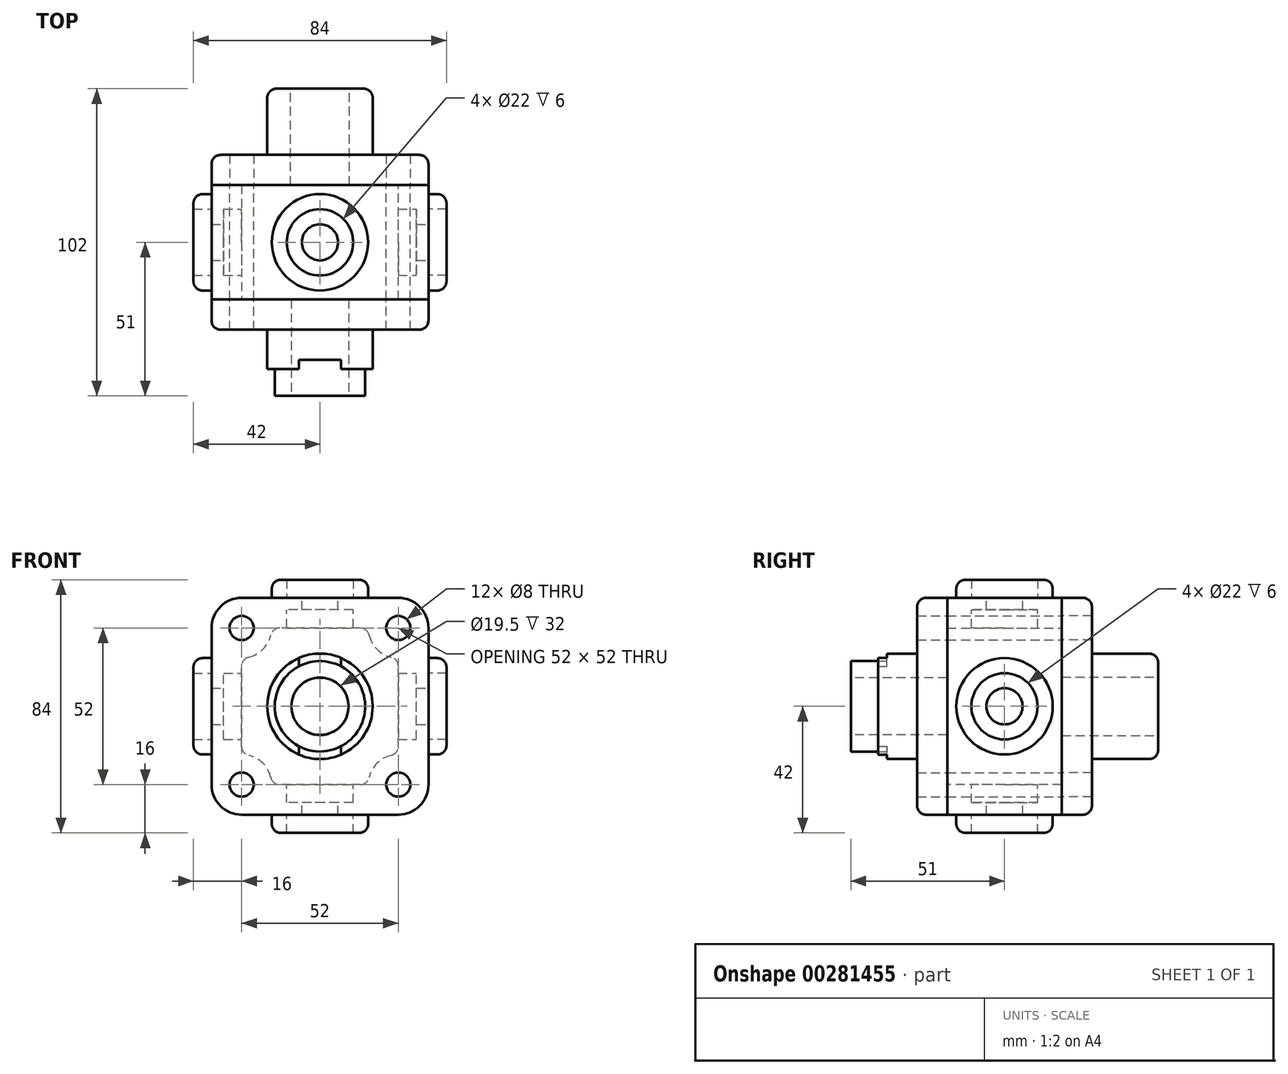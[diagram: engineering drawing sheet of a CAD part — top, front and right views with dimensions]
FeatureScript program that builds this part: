
annotation { "Feature Type Name" : "Feature", "Feature Type Description" : "" }
export const myFeature = defineFeature(function(context is Context, id is Id, definition is map)
    precondition{}
    {
        {
            var Q0;
            Q0=qCreatedBy(makeId("Front.planeOp"),FACE);
            var sketch = newSketch(context, id + "F0", { "sketchPlane" : qUnion([Q0])});
            skLineSegment(sketch, "E0.bottom", {"start": v(26, -26) * mm, "end": v(-26, -26) * mm});
            skLineSegment(sketch, "E0.top", {"start": v(26, 26) * mm, "end": v(-26, 26) * mm});
            skLineSegment(sketch, "E0.left", {"start": v(26, -26) * mm, "end": v(26, 26) * mm});
            skLineSegment(sketch, "E0.right", {"start": v(-26, -26) * mm, "end": v(-26, 26) * mm});
            skPoint(sketch, "E0.middle", {"position": v(0, 0) * mm});
            skLineSegment(sketch, "E1.bottom", {"start": v(-36, -36) * mm, "end": v(36, -36) * mm});
            skLineSegment(sketch, "E1.top", {"start": v(-36, 36) * mm, "end": v(36, 36) * mm});
            skLineSegment(sketch, "E1.left", {"start": v(-36, -36) * mm, "end": v(-36, 36) * mm});
            skLineSegment(sketch, "E1.right", {"start": v(36, -36) * mm, "end": v(36, 36) * mm});
            skCircle(sketch, "E2", {"center": v(26, 26) * mm, "radius": 10 * mm});
            skCircle(sketch, "E3", {"center": v(-26, 26) * mm, "radius": 10 * mm});
            skCircle(sketch, "E4", {"center": v(-26, -26) * mm, "radius": 10 * mm});
            skCircle(sketch, "E5", {"center": v(26, -26) * mm, "radius": 10 * mm});
            skLineSegment(sketch, "E6", {"start": v(36, 36) * mm, "end": v(-36, -36) * mm, "construction": true});
            skLineSegment(sketch, "E7", {"start": v(36, -36) * mm, "end": v(-36, 36) * mm, "construction": true});
            skCircle(sketch, "E8", {"center": v(26, 26) * mm, "radius": 4 * mm});
            skCircle(sketch, "E9", {"center": v(-26, 26) * mm, "radius": 4 * mm});
            skCircle(sketch, "E10", {"center": v(-26, -26) * mm, "radius": 4 * mm});
            skCircle(sketch, "E11", {"center": v(26, -26) * mm, "radius": 4 * mm});
            skLineSegment(sketch, "E12", {"start": v(-72.63, 0) * mm, "end": v(73.83, 0) * mm, "construction": true});
            skLineSegment(sketch, "E13", {"start": v(0, -65.86) * mm, "end": v(0, 72.71) * mm, "construction": true});
            skSolve(sketch);
        }
        {
            var Q0;
            {var subQ0=sQuery(id+"F0.wireOp",EDGE,"E5");var subQ3=makeQuery(id+"F0.imprint","INTERSECT",VERTEX,{"derivedFrom":[sQuery(id+"F0.wireOp",EDGE,"E1.bottom"),subQ0]});Q0=makeQuery(id+"F0.imprint","IMPRINT",FACE,{"disambiguationData":[TD([[makeQuery(id+"F0.imprint","IMPRINT",EDGE,{"disambiguationData":[TD([[subQ3,-1.0]])],"derivedFrom":subQ0}),1.0]])]});}
            var Q1;
            {var subQ0=sQuery(id+"F0.wireOp",EDGE,"E4");var subQ1=sQuery(id+"F0.wireOp",EDGE,"E1.bottom");var subQ2=makeQuery(id+"F0.imprint","INTERSECT",VERTEX,{"derivedFrom":[subQ1,subQ0]});Q1=makeQuery(id+"F0.imprint","IMPRINT",FACE,{"disambiguationData":[TD([[makeQuery(id+"F0.imprint","IMPRINT",EDGE,{"disambiguationData":[TD([[subQ2,-1.0]])],"derivedFrom":subQ1}),1.0]])]});}
            var Q2;
            {var subQ5=sQuery(id+"F0.wireOp",EDGE,"2c42fa13-fa19-4489-94e4-404aec46edff.top");Q2=makeQuery(id+"F0.imprint","IMPRINT",FACE,{"disambiguationData":[TD([[makeQuery(id+"F0.imprint","IMPRINT",EDGE,{"derivedFrom":subQ5}),1.0]])]});}
            var Q3;
            {var subQ5=sQuery(id+"F0.wireOp",EDGE,"ed80a6a9-9b49-4b89-9adc-e16e461cd2ad.left");Q3=makeQuery(id+"F0.imprint","IMPRINT",FACE,{"disambiguationData":[TD([[makeQuery(id+"F0.imprint","IMPRINT",EDGE,{"derivedFrom":subQ5}),1.0]])]});}
            var Q4;
            {var subQ0=sQuery(id+"F0.wireOp",EDGE,"E3");var subQ1=sQuery(id+"F0.wireOp",EDGE,"E1.top");var subQ2=makeQuery(id+"F0.imprint","INTERSECT",VERTEX,{"derivedFrom":[subQ1,subQ0]});Q4=makeQuery(id+"F0.imprint","IMPRINT",FACE,{"disambiguationData":[TD([[makeQuery(id+"F0.imprint","IMPRINT",EDGE,{"disambiguationData":[TD([[subQ2,-1.0]])],"derivedFrom":subQ1}),-1.0]])]});}
            var Q5;
            {var subQ0=sQuery(id+"F0.wireOp",EDGE,"E2");var subQ3=makeQuery(id+"F0.imprint","INTERSECT",VERTEX,{"derivedFrom":[sQuery(id+"F0.wireOp",EDGE,"E1.top"),subQ0]});Q5=makeQuery(id+"F0.imprint","IMPRINT",FACE,{"disambiguationData":[TD([[makeQuery(id+"F0.imprint","IMPRINT",EDGE,{"disambiguationData":[TD([[subQ3,1.0]])],"derivedFrom":subQ0}),1.0]])]});}
            var Q6;
            {var subQ5=sQuery(id+"F0.wireOp",EDGE,"43d30307-da37-4a26-9242-e517d63e6419.top");Q6=makeQuery(id+"F0.imprint","IMPRINT",FACE,{"disambiguationData":[TD([[makeQuery(id+"F0.imprint","IMPRINT",EDGE,{"derivedFrom":subQ5}),-1.0]])]});}
            var Q7;
            {var subQ0=sQuery(id+"F0.wireOp",EDGE,"E3");var subQ3=makeQuery(id+"F0.imprint","INTERSECT",VERTEX,{"derivedFrom":[sQuery(id+"F0.wireOp",EDGE,"E1.top"),subQ0]});Q7=makeQuery(id+"F0.imprint","IMPRINT",FACE,{"disambiguationData":[TD([[makeQuery(id+"F0.imprint","IMPRINT",EDGE,{"disambiguationData":[TD([[subQ3,-1.0]])],"derivedFrom":subQ0}),1.0]])]});}
            var Q8;
            {var subQ0=sQuery(id+"F0.wireOp",EDGE,"E4");var subQ1=sQuery(id+"F0.wireOp",EDGE,"E1.left");var subQ2=makeQuery(id+"F0.imprint","INTERSECT",VERTEX,{"derivedFrom":[subQ1,subQ0]});Q8=makeQuery(id+"F0.imprint","IMPRINT",FACE,{"disambiguationData":[TD([[makeQuery(id+"F0.imprint","IMPRINT",EDGE,{"disambiguationData":[TD([[subQ2,-1.0]])],"derivedFrom":subQ1}),-1.0]])]});}
            var Q9;
            {var subQ0=sQuery(id+"F0.wireOp",EDGE,"d46692bc-23da-4b0a-9166-fa2d0df1a2c0.right");Q9=makeQuery(id+"F0.imprint","IMPRINT",FACE,{"disambiguationData":[TD([[makeQuery(id+"F0.imprint","IMPRINT",EDGE,{"derivedFrom":subQ0}),1.0]])]});}
            var Q10;
            {var subQ0=sQuery(id+"F0.wireOp",EDGE,"E5");var subQ1=sQuery(id+"F0.wireOp",EDGE,"E1.right");var subQ2=makeQuery(id+"F0.imprint","INTERSECT",VERTEX,{"derivedFrom":[subQ1,subQ0]});Q10=makeQuery(id+"F0.imprint","IMPRINT",FACE,{"disambiguationData":[TD([[makeQuery(id+"F0.imprint","IMPRINT",EDGE,{"disambiguationData":[TD([[subQ2,-1.0]])],"derivedFrom":subQ1}),1.0]])]});}
            var Q11;
            {var subQ0=sQuery(id+"F0.wireOp",EDGE,"E4");var subQ1=makeQuery(id+"F0.imprint","INTERSECT",VERTEX,{"derivedFrom":[sQuery(id+"F0.wireOp",EDGE,"E1.bottom"),subQ0]});Q11=makeQuery(id+"F0.imprint","IMPRINT",FACE,{"disambiguationData":[TD([[makeQuery(id+"F0.imprint","IMPRINT",EDGE,{"disambiguationData":[TD([[subQ1,1.0]])],"derivedFrom":subQ0}),1.0]])]});}
            var Q12;
            {var subQ5=sQuery(id+"F0.wireOp",EDGE,"2c42fa13-fa19-4489-94e4-404aec46edff.bottom");Q12=makeQuery(id+"F0.imprint","IMPRINT",FACE,{"disambiguationData":[TD([[makeQuery(id+"F0.imprint","IMPRINT",EDGE,{"derivedFrom":subQ5}),-1.0]])]});}
            var Q13;
            {var subQ5=sQuery(id+"F0.wireOp",EDGE,"ed80a6a9-9b49-4b89-9adc-e16e461cd2ad.right");Q13=makeQuery(id+"F0.imprint","IMPRINT",FACE,{"disambiguationData":[TD([[makeQuery(id+"F0.imprint","IMPRINT",EDGE,{"derivedFrom":subQ5}),-1.0]])]});}
            var Q14;
            {var subQ5=sQuery(id+"F0.wireOp",EDGE,"d46692bc-23da-4b0a-9166-fa2d0df1a2c0.left");Q14=makeQuery(id+"F0.imprint","IMPRINT",FACE,{"disambiguationData":[TD([[makeQuery(id+"F0.imprint","IMPRINT",EDGE,{"derivedFrom":subQ5}),-1.0]])]});}
            var Q15;
            {var subQ5=sQuery(id+"F0.wireOp",EDGE,"43d30307-da37-4a26-9242-e517d63e6419.bottom");Q15=makeQuery(id+"F0.imprint","IMPRINT",FACE,{"disambiguationData":[TD([[makeQuery(id+"F0.imprint","IMPRINT",EDGE,{"derivedFrom":subQ5}),1.0]])]});}
            var Q16;
            {var subQ1=sQuery(id+"F0.wireOp",EDGE,"E0.top");var subQ3=sQuery(id+"F0.wireOp",EDGE,"E9");var subQ4=makeQuery(id+"F0.imprint","INTERSECT",VERTEX,{"derivedFrom":[subQ1,subQ3]});Q16=makeQuery(id+"F0.imprint","IMPRINT",FACE,{"disambiguationData":[TD([[makeQuery(id+"F0.imprint","IMPRINT",EDGE,{"disambiguationData":[TD([[subQ4,1.0]])],"derivedFrom":subQ3}),-1.0]])]});}
            var Q17;
            {var subQ1=sQuery(id+"F0.wireOp",EDGE,"E0.bottom");var subQ3=sQuery(id+"F0.wireOp",EDGE,"E10");var subQ4=makeQuery(id+"F0.imprint","INTERSECT",VERTEX,{"derivedFrom":[subQ1,subQ3]});Q17=makeQuery(id+"F0.imprint","IMPRINT",FACE,{"disambiguationData":[TD([[makeQuery(id+"F0.imprint","IMPRINT",EDGE,{"disambiguationData":[TD([[subQ4,-1.0]])],"derivedFrom":subQ3}),-1.0]])]});}
            var Q18;
            {var subQ1=sQuery(id+"F0.wireOp",EDGE,"E0.bottom");var subQ3=sQuery(id+"F0.wireOp",EDGE,"E11");var subQ4=makeQuery(id+"F0.imprint","INTERSECT",VERTEX,{"derivedFrom":[subQ1,subQ3]});Q18=makeQuery(id+"F0.imprint","IMPRINT",FACE,{"disambiguationData":[TD([[makeQuery(id+"F0.imprint","IMPRINT",EDGE,{"disambiguationData":[TD([[subQ4,1.0]])],"derivedFrom":subQ3}),-1.0]])]});}
            var Q19;
            {var subQ1=sQuery(id+"F0.wireOp",EDGE,"E0.top");var subQ3=sQuery(id+"F0.wireOp",EDGE,"E8");var subQ4=makeQuery(id+"F0.imprint","INTERSECT",VERTEX,{"derivedFrom":[subQ1,subQ3]});Q19=makeQuery(id+"F0.imprint","IMPRINT",FACE,{"disambiguationData":[TD([[makeQuery(id+"F0.imprint","IMPRINT",EDGE,{"disambiguationData":[TD([[subQ4,-1.0]])],"derivedFrom":subQ3}),-1.0]])]});}
            extrude(context, id + "F1", {"entities" : qUnion([Q0, Q1, Q2, Q3, Q4, Q5, Q6, Q7, Q8, Q9, Q10, Q11, Q12, Q13, Q14, Q15, Q16, Q17, Q18, Q19]), "endBound" : BoundingType.SYMMETRIC, "depth" : 38 * mm});
        }
        {
            var Q0;
            Q0=qCreatedBy(makeId("Right.planeOp"),FACE);
            var sketch = newSketch(context, id + "F2", { "sketchPlane" : qUnion([Q0])});
            skCircle(sketch, "E14", {"center": v(0, 0) * mm, "radius": 11 * mm});
            skCircle(sketch, "E15", {"center": v(0, 0) * mm, "radius": 6 * mm});
            skSolve(sketch);
        }
        {
            var Q0;
            Q0=makeQuery(id+"F2.imprint","IMPRINT",FACE,{"disambiguationData":[TD([[makeQuery(id+"F2.imprint","IMPRINT",EDGE,{"derivedFrom":sQuery(id+"F2.wireOp",EDGE,"E15")}),1.0]])]});
            extrude(context, id + "F3", {"entities" : qUnion([Q0]), "operationType" : NewBodyOperationType.REMOVE, "endBound" : BoundingType.SYMMETRIC, "oppositeDirection" : true, "depth" : 80 * mm});
        }
        {
            var Q0;
            Q0=makeQuery(id+"F2.imprint","IMPRINT",FACE,{"disambiguationData":[TD([[makeQuery(id+"F2.imprint","IMPRINT",EDGE,{"derivedFrom":sQuery(id+"F2.wireOp",EDGE,"E14")}),1.0]])]});
            extrude(context, id + "F4", {"entities" : qUnion([Q0]), "operationType" : NewBodyOperationType.REMOVE, "endBound" : BoundingType.SYMMETRIC, "oppositeDirection" : true, "depth" : 64 * mm});
        }
        {
            var Q0;
            Q0=makeQuery(id+"F1.opExtrude","SWEPT_FACE",FACE,{"disambiguationData":[OSD([sQuery(id+"F0.wireOp",EDGE,"E1.left")])]});
            var sketch = newSketch(context, id + "F5", { "sketchPlane" : qUnion([Q0])});
            skCircle(sketch, "E16", {"center": v(0, 0) * mm, "radius": 11 * mm});
            skCircle(sketch, "E17", {"center": v(0, 0) * mm, "radius": 16 * mm});
            skSolve(sketch);
        }
        {
            var Q0;
            Q0=makeQuery(id+"F5.imprint","IMPRINT",FACE,{"disambiguationData":[TD([[makeQuery(id+"F5.imprint","IMPRINT",EDGE,{"derivedFrom":sQuery(id+"F5.wireOp",EDGE,"E16")}),-1.0]])]});
            extrude(context, id + "F6", {"entities" : qUnion([Q0]), "operationType" : NewBodyOperationType.ADD, "depth" : 6 * mm});
        }
        {
            var Q0;
            Q0=makeQuery(id+"F1.opExtrude","SWEPT_FACE",FACE,{"disambiguationData":[OSD([sQuery(id+"F0.wireOp",EDGE,"E1.right")])]});
            var sketch = newSketch(context, id + "F7", { "sketchPlane" : qUnion([Q0])});
            skCircle(sketch, "E18", {"center": v(0, 0) * mm, "radius": 11 * mm});
            skCircle(sketch, "E19", {"center": v(0, 0) * mm, "radius": 16 * mm});
            skSolve(sketch);
        }
        {
            var Q0;
            Q0=makeQuery(id+"F7.imprint","IMPRINT",FACE,{"disambiguationData":[TD([[makeQuery(id+"F7.imprint","IMPRINT",EDGE,{"derivedFrom":sQuery(id+"F7.wireOp",EDGE,"E18")}),-1.0]])]});
            extrude(context, id + "F8", {"entities" : qUnion([Q0]), "operationType" : NewBodyOperationType.ADD, "depth" : 6 * mm});
        }
        {
            var Q0;
            Q0=qCreatedBy(makeId("Top.planeOp"),FACE);
            var sketch = newSketch(context, id + "F9", { "sketchPlane" : qUnion([Q0])});
            skCircle(sketch, "E20", {"center": v(0, 0) * mm, "radius": 6 * mm});
            skCircle(sketch, "E21", {"center": v(0, 0) * mm, "radius": 11 * mm});
            skSolve(sketch);
        }
        {
            var Q0;
            Q0=makeQuery(id+"F9.imprint","IMPRINT",FACE,{"disambiguationData":[TD([[makeQuery(id+"F9.imprint","IMPRINT",EDGE,{"derivedFrom":sQuery(id+"F9.wireOp",EDGE,"E20")}),1.0]])]});
            extrude(context, id + "F10", {"entities" : qUnion([Q0]), "operationType" : NewBodyOperationType.REMOVE, "endBound" : BoundingType.SYMMETRIC, "oppositeDirection" : true, "depth" : 80 * mm});
        }
        {
            var Q0;
            Q0=makeQuery(id+"F9.imprint","IMPRINT",FACE,{"disambiguationData":[TD([[makeQuery(id+"F9.imprint","IMPRINT",EDGE,{"derivedFrom":sQuery(id+"F9.wireOp",EDGE,"E20")}),-1.0]])]});
            extrude(context, id + "F11", {"entities" : qUnion([Q0]), "operationType" : NewBodyOperationType.REMOVE, "endBound" : BoundingType.SYMMETRIC, "oppositeDirection" : true, "depth" : 64 * mm});
        }
        {
            var Q0;
            Q0=makeQuery(id+"F1.opExtrude","SWEPT_FACE",FACE,{"disambiguationData":[OSD([sQuery(id+"F0.wireOp",EDGE,"E1.top")])]});
            var sketch = newSketch(context, id + "F12", { "sketchPlane" : qUnion([Q0])});
            skCircle(sketch, "E22", {"center": v(0, 0) * mm, "radius": 11 * mm});
            skCircle(sketch, "E23", {"center": v(0, 0) * mm, "radius": 16 * mm});
            skSolve(sketch);
        }
        {
            var Q0;
            Q0=makeQuery(id+"F12.imprint","IMPRINT",FACE,{"disambiguationData":[TD([[makeQuery(id+"F12.imprint","IMPRINT",EDGE,{"derivedFrom":sQuery(id+"F12.wireOp",EDGE,"E22")}),-1.0]])]});
            extrude(context, id + "F13", {"entities" : qUnion([Q0]), "operationType" : NewBodyOperationType.ADD, "depth" : 6 * mm});
        }
        {
            var Q0;
            Q0=makeQuery(id+"F1.opExtrude","SWEPT_FACE",FACE,{"disambiguationData":[OSD([sQuery(id+"F0.wireOp",EDGE,"E1.bottom")])]});
            var sketch = newSketch(context, id + "F14", { "sketchPlane" : qUnion([Q0])});
            skCircle(sketch, "E24", {"center": v(0, 0) * mm, "radius": 11 * mm});
            skCircle(sketch, "E25", {"center": v(0, 0) * mm, "radius": 16 * mm});
            skSolve(sketch);
        }
        {
            var Q0;
            Q0=makeQuery(id+"F14.imprint","IMPRINT",FACE,{"disambiguationData":[TD([[makeQuery(id+"F14.imprint","IMPRINT",EDGE,{"derivedFrom":sQuery(id+"F14.wireOp",EDGE,"E24")}),-1.0]])]});
            extrude(context, id + "F15", {"entities" : qUnion([Q0]), "operationType" : NewBodyOperationType.ADD, "depth" : 6 * mm});
        }
        {
            var Q0;
            Q0=makeQuery(id+"F15.opExtrude","CAP_EDGE",EDGE,{"disambiguationData":[OSD([sQuery(id+"F14.wireOp",EDGE,"E25")])],"isStart":true});
            var Q1;
            Q1=makeQuery(id+"F6.opExtrude","CAP_EDGE",EDGE,{"disambiguationData":[OSD([sQuery(id+"F5.wireOp",EDGE,"E17")])],"isStart":true});
            var Q2;
            Q2=makeQuery(id+"F8.opExtrude","CAP_EDGE",EDGE,{"disambiguationData":[OSD([sQuery(id+"F7.wireOp",EDGE,"E19")])],"isStart":true});
            var Q3;
            Q3=makeQuery(id+"F13.opExtrude","CAP_EDGE",EDGE,{"disambiguationData":[OSD([sQuery(id+"F12.wireOp",EDGE,"E23")])],"isStart":true});
            var Q4;
            Q4=makeQuery(id+"F1.opExtrude","SWEPT_EDGE",EDGE,{"disambiguationData":[OSD([sQuery(id+"F0.wireOp",EDGE,"E0.right"),sQuery(id+"F0.wireOp",EDGE,"E4")])]});
            var Q5;
            Q5=makeQuery(id+"F1.opExtrude","SWEPT_EDGE",EDGE,{"disambiguationData":[OSD([sQuery(id+"F0.wireOp",EDGE,"E0.bottom"),sQuery(id+"F0.wireOp",EDGE,"E4")])]});
            var Q6;
            Q6=makeQuery(id+"F1.opExtrude","SWEPT_EDGE",EDGE,{"disambiguationData":[OSD([sQuery(id+"F0.wireOp",EDGE,"E0.left"),sQuery(id+"F0.wireOp",EDGE,"E5")])]});
            var Q7;
            Q7=makeQuery(id+"F1.opExtrude","SWEPT_EDGE",EDGE,{"disambiguationData":[OSD([sQuery(id+"F0.wireOp",EDGE,"E0.bottom"),sQuery(id+"F0.wireOp",EDGE,"E5")])]});
            var Q8;
            Q8=makeQuery(id+"F1.opExtrude","SWEPT_EDGE",EDGE,{"disambiguationData":[OSD([sQuery(id+"F0.wireOp",EDGE,"E0.left"),sQuery(id+"F0.wireOp",EDGE,"E2")])]});
            var Q9;
            Q9=makeQuery(id+"F1.opExtrude","SWEPT_EDGE",EDGE,{"disambiguationData":[OSD([sQuery(id+"F0.wireOp",EDGE,"E0.top"),sQuery(id+"F0.wireOp",EDGE,"E2")])]});
            var Q10;
            Q10=makeQuery(id+"F1.opExtrude","SWEPT_EDGE",EDGE,{"disambiguationData":[OSD([sQuery(id+"F0.wireOp",EDGE,"E0.top"),sQuery(id+"F0.wireOp",EDGE,"E3")])]});
            var Q11;
            Q11=makeQuery(id+"F1.opExtrude","SWEPT_EDGE",EDGE,{"disambiguationData":[OSD([sQuery(id+"F0.wireOp",EDGE,"E0.right"),sQuery(id+"F0.wireOp",EDGE,"E3")])]});
            var Q12;
            Q12=makeQuery(id+"F8.opExtrude","CAP_EDGE",EDGE,{"disambiguationData":[OSD([sQuery(id+"F7.wireOp",EDGE,"E19")])],"isStart":false});
            var Q13;
            Q13=makeQuery(id+"F15.opExtrude","CAP_EDGE",EDGE,{"disambiguationData":[OSD([sQuery(id+"F14.wireOp",EDGE,"E25")])],"isStart":false});
            var Q14;
            Q14=makeQuery(id+"F13.opExtrude","CAP_EDGE",EDGE,{"disambiguationData":[OSD([sQuery(id+"F12.wireOp",EDGE,"E23")])],"isStart":false});
            var Q15;
            Q15=makeQuery(id+"F6.opExtrude","CAP_EDGE",EDGE,{"disambiguationData":[OSD([sQuery(id+"F5.wireOp",EDGE,"E17")])],"isStart":false});
            fillet(context, id + "F16", {"entities" : qUnion([Q0, Q1, Q2, Q3, Q4, Q5, Q6, Q7, Q8, Q9, Q10, Q11, Q12, Q13, Q14, Q15]), "radius" : 3 * mm, "tangentPropagation" : true, "allowEdgeOverflow" : false});
        }
        {
            var Q0;
            Q0=makeQuery(id+"F1.opExtrude","CAP_FACE",FACE,{"disambiguationData":[OSD([sQuery(id+"F0.wireOp",EDGE,"E0.bottom"),sQuery(id+"F0.wireOp",EDGE,"E0.top"),sQuery(id+"F0.wireOp",EDGE,"E0.left"),sQuery(id+"F0.wireOp",EDGE,"E0.right"),sQuery(id+"F0.wireOp",EDGE,"E1.bottom"),sQuery(id+"F0.wireOp",EDGE,"E1.top"),sQuery(id+"F0.wireOp",EDGE,"E1.left"),sQuery(id+"F0.wireOp",EDGE,"E1.right"),sQuery(id+"F0.wireOp",EDGE,"E2"),sQuery(id+"F0.wireOp",EDGE,"E3"),sQuery(id+"F0.wireOp",EDGE,"E4"),sQuery(id+"F0.wireOp",EDGE,"E5"),sQuery(id+"F0.wireOp",EDGE,"E8"),sQuery(id+"F0.wireOp",EDGE,"E9"),sQuery(id+"F0.wireOp",EDGE,"E10"),sQuery(id+"F0.wireOp",EDGE,"E11")])],"isStart":false});
            var sketch = newSketch(context, id + "F17", { "sketchPlane" : qUnion([Q0])});
            skSolve(sketch);
        }
        {
            var Q0;
            {var subQ1=sQuery(id+"F0.wireOp",EDGE,"E0.bottom");Q0=makeQuery(id+"F17.imprint","IMPRINT",FACE,{"disambiguationData":[TD([[makeQuery(id+"F17.imprint","IMPRINT",EDGE,{"derivedFrom":makeQuery(id+"F1.opExtrude","CAP_EDGE",EDGE,{"disambiguationData":[OSD([subQ1])],"isStart":false})}),-1.0]])]});}
            var Q1;
            {var subQ11=sQuery(id+"F0.wireOp",EDGE,"E8");Q1=makeQuery(id+"F17.imprint","IMPRINT",FACE,{"disambiguationData":[TD([[makeQuery(id+"F17.imprint","IMPRINT",EDGE,{"derivedFrom":makeQuery(id+"F1.opExtrude","CAP_EDGE",EDGE,{"disambiguationData":[OSD([subQ11])],"isStart":false})}),-1.0]])]});}
            extrude(context, id + "F18", {"entities" : qUnion([Q0, Q1]), "depth" : 10 * mm});
        }
        {
            var Q0;
            Q0=makeQuery(id+"F18.opExtrude","CAP_FACE",FACE,{"disambiguationData":[OSD([sQuery(id+"F0.wireOp",EDGE,"E1.bottom"),sQuery(id+"F0.wireOp",EDGE,"E1.top"),sQuery(id+"F0.wireOp",EDGE,"E1.left"),sQuery(id+"F0.wireOp",EDGE,"E1.right"),sQuery(id+"F0.wireOp",EDGE,"E2"),sQuery(id+"F0.wireOp",EDGE,"E3"),sQuery(id+"F0.wireOp",EDGE,"E4"),sQuery(id+"F0.wireOp",EDGE,"E5"),sQuery(id+"F0.wireOp",EDGE,"E8"),sQuery(id+"F0.wireOp",EDGE,"E9"),sQuery(id+"F0.wireOp",EDGE,"E10"),sQuery(id+"F0.wireOp",EDGE,"E11")])],"isStart":false});
            var sketch = newSketch(context, id + "F19", { "sketchPlane" : qUnion([Q0])});
            skCircle(sketch, "E26", {"center": v(0, 0) * mm, "radius": 9.5 * mm});
            skCircle(sketch, "E27", {"center": v(0, 0) * mm, "radius": 15 * mm});
            skCircle(sketch, "E28", {"center": v(0, 0) * mm, "radius": 17.5 * mm});
            skSolve(sketch);
        }
        {
            var Q0;
            Q0=makeQuery(id+"F19.imprint","IMPRINT",FACE,{"disambiguationData":[TD([[makeQuery(id+"F19.imprint","IMPRINT",EDGE,{"derivedFrom":sQuery(id+"F19.wireOp",EDGE,"E26")}),1.0]])]});
            extrude(context, id + "F20", {"entities" : qUnion([Q0]), "operationType" : NewBodyOperationType.REMOVE, "oppositeDirection" : true, "depth" : 10 * mm});
        }
        {
            var Q0;
            Q0=makeQuery(id+"F19.imprint","IMPRINT",FACE,{"disambiguationData":[TD([[makeQuery(id+"F19.imprint","IMPRINT",EDGE,{"derivedFrom":sQuery(id+"F19.wireOp",EDGE,"E26")}),1.0]])]});
            extrude(context, id + "F21", {"entities" : qUnion([Q0]), "operationType" : NewBodyOperationType.REMOVE, "oppositeDirection" : true, "depth" : 10 * mm});
        }
        {
            var Q0;
            Q0=makeQuery(id+"F19.imprint","IMPRINT",FACE,{"disambiguationData":[TD([[makeQuery(id+"F19.imprint","IMPRINT",EDGE,{"derivedFrom":sQuery(id+"F19.wireOp",EDGE,"E26")}),-1.0]])]});
            extrude(context, id + "F22", {"entities" : qUnion([Q0]), "operationType" : NewBodyOperationType.ADD, "depth" : 22 * mm});
        }
        {
            var Q0;
            Q0=makeQuery(id+"F19.imprint","IMPRINT",FACE,{"disambiguationData":[TD([[makeQuery(id+"F19.imprint","IMPRINT",EDGE,{"derivedFrom":sQuery(id+"F19.wireOp",EDGE,"E27")}),-1.0]])]});
            extrude(context, id + "F23", {"entities" : qUnion([Q0]), "operationType" : NewBodyOperationType.ADD, "depth" : 10 * mm});
        }
        {
            var Q0;
            Q0=makeQuery(id+"F23.opExtrude","CAP_FACE",FACE,{"disambiguationData":[OSD([sQuery(id+"F19.wireOp",EDGE,"E27"),sQuery(id+"F19.wireOp",EDGE,"E28")])],"isStart":false});
            var sketch = newSketch(context, id + "F24", { "sketchPlane" : qUnion([Q0])});
            skLineSegment(sketch, "E29.bottom", {"start": v(7, -30) * mm, "end": v(-7, -30) * mm});
            skLineSegment(sketch, "E29.top", {"start": v(7, 30) * mm, "end": v(-7, 30) * mm});
            skLineSegment(sketch, "E29.left", {"start": v(7, -30) * mm, "end": v(7, 30) * mm});
            skLineSegment(sketch, "E29.right", {"start": v(-7, -30) * mm, "end": v(-7, 30) * mm});
            skPoint(sketch, "E29.middle", {"position": v(0, 0) * mm});
            skSolve(sketch);
        }
        {
            var Q0;
            {var subQ0=sQuery(id+"F24.wireOp",EDGE,"E29.left");var subQ1=makeQuery(id+"F23.opExtrude","CAP_EDGE",EDGE,{"disambiguationData":[OSD([sQuery(id+"F19.wireOp",EDGE,"E28")])],"isStart":false});var subQ2=makeQuery(id+"F24.imprint","INTERSECT",VERTEX,{"disambiguationData":[OD(0.0)],"derivedFrom":[subQ1,subQ0]});Q0=makeQuery(id+"F24.imprint","IMPRINT",FACE,{"disambiguationData":[TD([[makeQuery(id+"F24.imprint","IMPRINT",EDGE,{"disambiguationData":[TD([[subQ2,-1.0]])],"derivedFrom":subQ0}),-1.0]])]});}
            var Q1;
            {var subQ0=sQuery(id+"F24.wireOp",EDGE,"E29.right");var subQ1=makeQuery(id+"F23.opExtrude","CAP_EDGE",EDGE,{"disambiguationData":[OSD([sQuery(id+"F19.wireOp",EDGE,"E28")])],"isStart":false});var subQ2=makeQuery(id+"F24.imprint","INTERSECT",VERTEX,{"disambiguationData":[OD(0.0)],"derivedFrom":[subQ1,subQ0]});Q1=makeQuery(id+"F24.imprint","IMPRINT",FACE,{"disambiguationData":[TD([[makeQuery(id+"F24.imprint","IMPRINT",EDGE,{"disambiguationData":[TD([[subQ2,-1.0]])],"derivedFrom":subQ0}),1.0]])]});}
            extrude(context, id + "F25", {"entities" : qUnion([Q0, Q1]), "operationType" : NewBodyOperationType.ADD, "depth" : 3 * mm});
        }
        {
            var Q0;
            Q0=makeQuery(id+"F18.opExtrude","CAP_EDGE",EDGE,{"disambiguationData":[OSD([sQuery(id+"F0.wireOp",EDGE,"E1.right")])],"isStart":false});
            var Q1;
            Q1=makeQuery(id+"F18.opExtrude","CAP_EDGE",EDGE,{"disambiguationData":[OSD([sQuery(id+"F0.wireOp",EDGE,"E5")])],"isStart":false});
            var Q2;
            Q2=makeQuery(id+"F18.opExtrude","CAP_EDGE",EDGE,{"disambiguationData":[OSD([sQuery(id+"F0.wireOp",EDGE,"E2")])],"isStart":false});
            var Q3;
            Q3=makeQuery(id+"F18.opExtrude","CAP_EDGE",EDGE,{"disambiguationData":[OSD([sQuery(id+"F0.wireOp",EDGE,"E1.top")])],"isStart":false});
            var Q4;
            Q4=makeQuery(id+"F18.opExtrude","CAP_EDGE",EDGE,{"disambiguationData":[OSD([sQuery(id+"F0.wireOp",EDGE,"E3")])],"isStart":false});
            var Q5;
            Q5=makeQuery(id+"F18.opExtrude","CAP_EDGE",EDGE,{"disambiguationData":[OSD([sQuery(id+"F0.wireOp",EDGE,"E1.left")])],"isStart":false});
            var Q6;
            Q6=makeQuery(id+"F18.opExtrude","CAP_EDGE",EDGE,{"disambiguationData":[OSD([sQuery(id+"F0.wireOp",EDGE,"E1.bottom")])],"isStart":false});
            var Q7;
            Q7=makeQuery(id+"F18.opExtrude","CAP_EDGE",EDGE,{"disambiguationData":[OSD([sQuery(id+"F0.wireOp",EDGE,"E4")])],"isStart":false});
            fillet(context, id + "F26", {"entities" : qUnion([Q0, Q1, Q2, Q3, Q4, Q5, Q6, Q7]), "radius" : 3 * mm, "tangentPropagation" : true, "allowEdgeOverflow" : false});
        }
        {
            var Q0;
            Q0=makeQuery(id+"F1.opExtrude","CAP_FACE",FACE,{"disambiguationData":[OSD([sQuery(id+"F0.wireOp",EDGE,"E0.bottom"),sQuery(id+"F0.wireOp",EDGE,"E0.top"),sQuery(id+"F0.wireOp",EDGE,"E0.left"),sQuery(id+"F0.wireOp",EDGE,"E0.right"),sQuery(id+"F0.wireOp",EDGE,"E1.bottom"),sQuery(id+"F0.wireOp",EDGE,"E1.top"),sQuery(id+"F0.wireOp",EDGE,"E1.left"),sQuery(id+"F0.wireOp",EDGE,"E1.right"),sQuery(id+"F0.wireOp",EDGE,"E2"),sQuery(id+"F0.wireOp",EDGE,"E3"),sQuery(id+"F0.wireOp",EDGE,"E4"),sQuery(id+"F0.wireOp",EDGE,"E5"),sQuery(id+"F0.wireOp",EDGE,"E8"),sQuery(id+"F0.wireOp",EDGE,"E9"),sQuery(id+"F0.wireOp",EDGE,"E10"),sQuery(id+"F0.wireOp",EDGE,"E11")])],"isStart":true});
            var sketch = newSketch(context, id + "F27", { "sketchPlane" : qUnion([Q0])});
            skSolve(sketch);
        }
        {
            var Q0;
            {var subQ11=sQuery(id+"F0.wireOp",EDGE,"E8");Q0=makeQuery(id+"F27.imprint","IMPRINT",FACE,{"disambiguationData":[TD([[makeQuery(id+"F27.imprint","IMPRINT",EDGE,{"derivedFrom":makeQuery(id+"F1.opExtrude","CAP_EDGE",EDGE,{"disambiguationData":[OSD([subQ11])],"isStart":true})}),1.0]])]});}
            var Q1;
            {var subQ1=sQuery(id+"F0.wireOp",EDGE,"E0.bottom");Q1=makeQuery(id+"F27.imprint","IMPRINT",FACE,{"disambiguationData":[TD([[makeQuery(id+"F27.imprint","IMPRINT",EDGE,{"derivedFrom":makeQuery(id+"F1.opExtrude","CAP_EDGE",EDGE,{"disambiguationData":[OSD([subQ1])],"isStart":true})}),1.0]])]});}
            extrude(context, id + "F28", {"entities" : qUnion([Q0, Q1]), "depth" : 10 * mm});
        }
        {
            var Q0;
            Q0=makeQuery(id+"F28.opExtrude","CAP_FACE",FACE,{"disambiguationData":[OSD([sQuery(id+"F0.wireOp",EDGE,"E1.bottom"),sQuery(id+"F0.wireOp",EDGE,"E1.top"),sQuery(id+"F0.wireOp",EDGE,"E1.left"),sQuery(id+"F0.wireOp",EDGE,"E1.right"),sQuery(id+"F0.wireOp",EDGE,"E2"),sQuery(id+"F0.wireOp",EDGE,"E3"),sQuery(id+"F0.wireOp",EDGE,"E4"),sQuery(id+"F0.wireOp",EDGE,"E5"),sQuery(id+"F0.wireOp",EDGE,"E8"),sQuery(id+"F0.wireOp",EDGE,"E9"),sQuery(id+"F0.wireOp",EDGE,"E10"),sQuery(id+"F0.wireOp",EDGE,"E11")])],"isStart":false});
            var sketch = newSketch(context, id + "F29", { "sketchPlane" : qUnion([Q0])});
            skCircle(sketch, "E30", {"center": v(0, 0) * mm, "radius": 9.75 * mm});
            skCircle(sketch, "E31", {"center": v(0, 0) * mm, "radius": 17.5 * mm});
            skSolve(sketch);
        }
        {
            var Q0;
            Q0=makeQuery(id+"F29.imprint","IMPRINT",FACE,{"disambiguationData":[TD([[makeQuery(id+"F29.imprint","IMPRINT",EDGE,{"derivedFrom":sQuery(id+"F29.wireOp",EDGE,"E30")}),1.0]])]});
            extrude(context, id + "F30", {"entities" : qUnion([Q0]), "operationType" : NewBodyOperationType.REMOVE, "oppositeDirection" : true, "depth" : 10 * mm});
        }
        {
            var Q0;
            Q0=makeQuery(id+"F29.imprint","IMPRINT",FACE,{"disambiguationData":[TD([[makeQuery(id+"F29.imprint","IMPRINT",EDGE,{"derivedFrom":sQuery(id+"F29.wireOp",EDGE,"E30")}),-1.0]])]});
            extrude(context, id + "F31", {"entities" : qUnion([Q0]), "operationType" : NewBodyOperationType.ADD, "depth" : 22 * mm});
        }
        {
            var Q0;
            Q0=makeQuery(id+"F28.opExtrude","CAP_EDGE",EDGE,{"disambiguationData":[OSD([sQuery(id+"F0.wireOp",EDGE,"E1.left")])],"isStart":false});
            var Q1;
            Q1=makeQuery(id+"F28.opExtrude","CAP_EDGE",EDGE,{"disambiguationData":[OSD([sQuery(id+"F0.wireOp",EDGE,"E4")])],"isStart":false});
            var Q2;
            Q2=makeQuery(id+"F28.opExtrude","CAP_EDGE",EDGE,{"disambiguationData":[OSD([sQuery(id+"F0.wireOp",EDGE,"E3")])],"isStart":false});
            var Q3;
            Q3=makeQuery(id+"F28.opExtrude","CAP_EDGE",EDGE,{"disambiguationData":[OSD([sQuery(id+"F0.wireOp",EDGE,"E1.top")])],"isStart":false});
            var Q4;
            Q4=makeQuery(id+"F31.opExtrude","CAP_EDGE",EDGE,{"disambiguationData":[OSD([sQuery(id+"F29.wireOp",EDGE,"E31")])],"isStart":false});
            var Q5;
            Q5=makeQuery(id+"F28.opExtrude","CAP_EDGE",EDGE,{"disambiguationData":[OSD([sQuery(id+"F0.wireOp",EDGE,"E2")])],"isStart":false});
            var Q6;
            Q6=makeQuery(id+"F28.opExtrude","CAP_EDGE",EDGE,{"disambiguationData":[OSD([sQuery(id+"F0.wireOp",EDGE,"E1.right")])],"isStart":false});
            var Q7;
            Q7=makeQuery(id+"F28.opExtrude","CAP_EDGE",EDGE,{"disambiguationData":[OSD([sQuery(id+"F0.wireOp",EDGE,"E1.bottom")])],"isStart":false});
            var Q8;
            Q8=makeQuery(id+"F28.opExtrude","CAP_EDGE",EDGE,{"disambiguationData":[OSD([sQuery(id+"F0.wireOp",EDGE,"E5")])],"isStart":false});
            fillet(context, id + "F32", {"entities" : qUnion([Q0, Q1, Q2, Q3, Q4, Q5, Q6, Q7, Q8]), "radius" : 3 * mm, "tangentPropagation" : true, "allowEdgeOverflow" : false});
        }
    });
